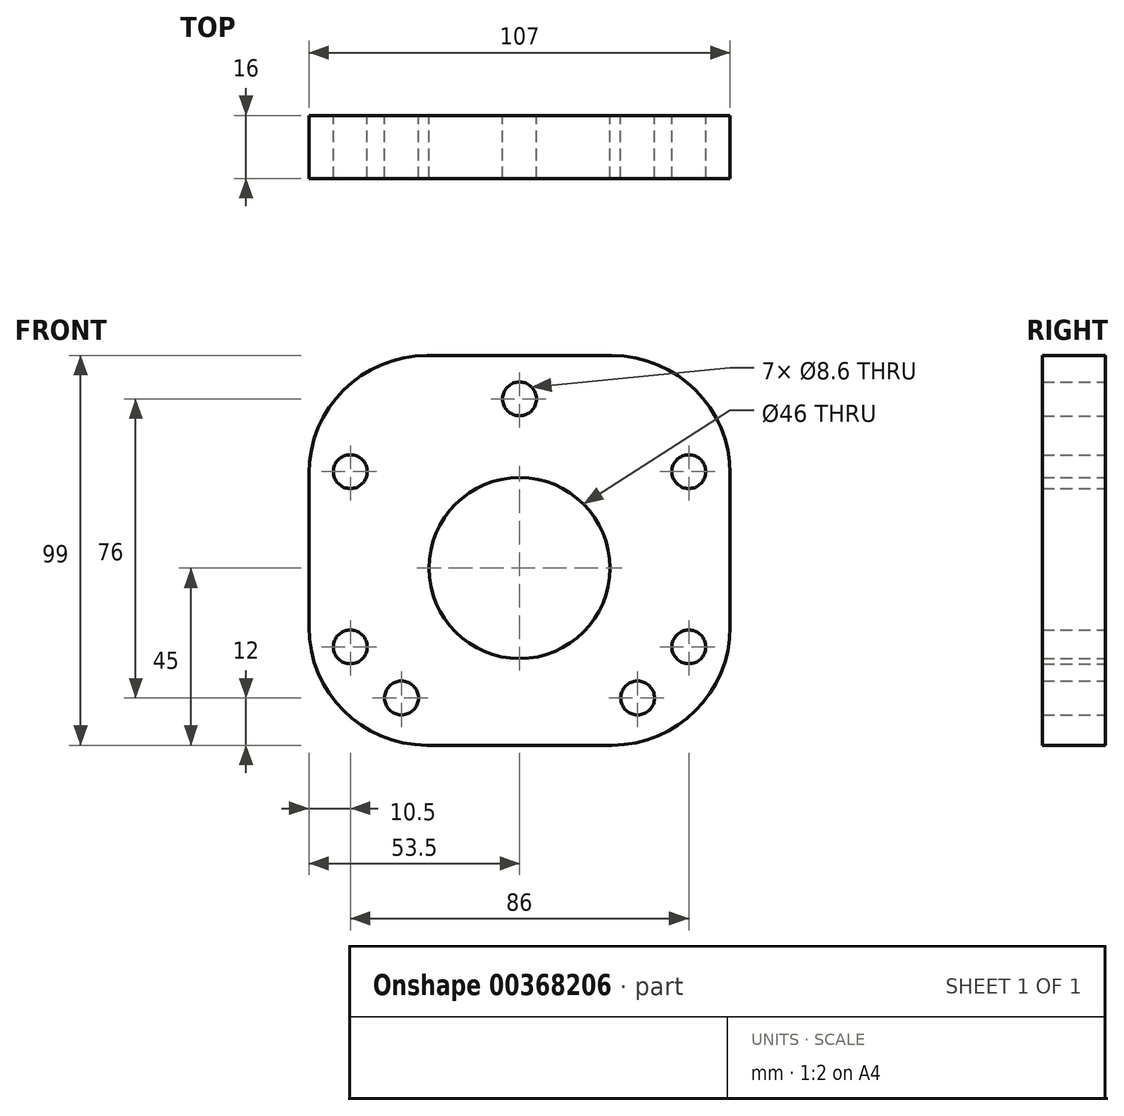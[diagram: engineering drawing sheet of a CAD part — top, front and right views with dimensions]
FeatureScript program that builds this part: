
annotation { "Feature Type Name" : "Feature", "Feature Type Description" : "" }
export const myFeature = defineFeature(function(context is Context, id is Id, definition is map)
    precondition{}
    {
        {
            var Q0;
            Q0=qCreatedBy(makeId("Front.planeOp"),FACE);
            var sketch = newSketch(context, id + "F0", { "sketchPlane" : qUnion([Q0])});
            skCircle(sketch, "E0", {"center": v(0, 0) * mm, "radius": 23 * mm});
            skLineSegment(sketch, "E1.bottom", {"start": v(-23.5, 54) * mm, "end": v(23.5, 54) * mm});
            skLineSegment(sketch, "E1.top", {"start": v(-23.5, -45) * mm, "end": v(23.5, -45) * mm});
            skLineSegment(sketch, "E1.left", {"start": v(-53.5, 24) * mm, "end": v(-53.5, -15) * mm});
            skLineSegment(sketch, "E1.right", {"start": v(53.5, 24) * mm, "end": v(53.5, -15) * mm});
            skCircle(sketch, "E2", {"center": v(30, -33) * mm, "radius": 4.3 * mm});
            skCircle(sketch, "E3", {"center": v(-30, -33) * mm, "radius": 4.3 * mm});
            skCircle(sketch, "E4", {"center": v(0, 43) * mm, "radius": 4.3 * mm});
            skCircle(sketch, "E5", {"center": v(43, -20) * mm, "radius": 4.3 * mm});
            skCircle(sketch, "E6", {"center": v(43, 24.5) * mm, "radius": 4.3 * mm});
            skCircle(sketch, "E7", {"center": v(-43, 24.5) * mm, "radius": 4.3 * mm});
            skCircle(sketch, "E8", {"center": v(-43, -20) * mm, "radius": 4.3 * mm});
            skPoint(sketch, "E9.visualSharp", {"position": v(-53.5, 54) * mm});
            skArc(sketch, "E9.filletArc", {"start": v(-23.5, 54) * mm, "mid": v(-44.71, 45.21) * mm, "end": v(-53.5, 24) * mm});
            skPoint(sketch, "E10.visualSharp", {"position": v(-53.5, -45) * mm});
            skArc(sketch, "E10.filletArc", {"start": v(-53.5, -15) * mm, "mid": v(-44.71, -36.21) * mm, "end": v(-23.5, -45) * mm});
            skPoint(sketch, "E11.visualSharp", {"position": v(53.5, -45) * mm});
            skArc(sketch, "E11.filletArc", {"start": v(23.5, -45) * mm, "mid": v(44.71, -36.21) * mm, "end": v(53.5, -15) * mm});
            skPoint(sketch, "E12.visualSharp", {"position": v(53.5, 54) * mm});
            skArc(sketch, "E12.filletArc", {"start": v(53.5, 24) * mm, "mid": v(44.71, 45.21) * mm, "end": v(23.5, 54) * mm});
            skSolve(sketch);
        }
        {
            var Q0;
            Q0=makeQuery(id+"F0.imprint","IMPRINT",FACE,{"disambiguationData":[TD([[makeQuery(id+"F0.imprint","IMPRINT",EDGE,{"derivedFrom":sQuery(id+"F0.wireOp",EDGE,"E0")}),-1.0]])]});
            extrude(context, id + "F1", {"entities" : qUnion([Q0]), "depth" : 16 * mm});
        }
    });
